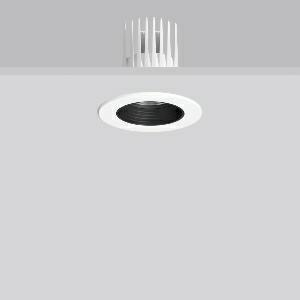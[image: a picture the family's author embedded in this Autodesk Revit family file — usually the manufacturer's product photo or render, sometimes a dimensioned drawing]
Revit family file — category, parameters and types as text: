
# Revit family: heledon_mini_e_901745_002_1_7fe4
name_source: partatom
category: Lighting Fixtures
units: mm (PartAtom-declared; Revit-internal decimal feet)

## family parameters
Cut with Voids When Loaded = No
Host = Face
Light Source = No
Part Type = Normal
Room Calculation Point = No
Round Connector Dimension = Use Diameter
Shared = No

## types (1)
- HELEDON mini E (1 x LED Modul 940, 2150 lm, 4000)
    Apparent Load = 20 VA
    Approval mark = CE
    CIE Flux Codes = 98 100 100 100 100
    Color Rendering = 92
    Color Temperature = 4000
    Default Elevation = 1800 mm
    Description = Series: HELEDON mini
Round recessed downlight. Housing: die-cast aluminium, powder-coated. Black plastic ring and recessed LED to prevent glare from the side. Optical assembly with lens made of plastic (polycarbonate) for the best homogeneous light distribution - can be changed without tools. Best colour rendering index Ra>90. Suitable for Recessed ceiling mounting. Installation without tools thanks to spring fastening system. Including separate LED converter with connecting cable 600 mm.High quality converter without flickering and stroboscopic effect. Through-wiring box (5 pole) available as accessory. The following accessories can be mounted without use of tools: interchangeable lenses, decorative glasses, honeycomb louvre, clear and frosted diffusers, white interchangeable plastic ring. 
Colour: traffic white, matt (RAL 9016)
Diameter: 124 mm
Height: 3 mm
Cut-out diameter: 114 mm
Recess height: 170 mm
Luminaire: recess height: 120 mm
Lamp: LED
Socket: without socket
Colour temperature: 4000K
Colour rendering index (CRI): 92
System power: 20 W
Rated luminous flux: 2150 lm
Luminous efficiency: 108 lm/W
Control gear: Regulated power supply
Protection class: II
Type of protection: IP 20
    Height = 0 mm  [stored 0 ft]
    Lamp = 1 x LED Modul 940
    Lamp Light Flux = 2150 lm
    Lamp count = 1
    Length = 124 mm  [stored 0.406824 ft]
    Lifetime = 50000 h
    Luminous efficacy = 108 lm/W
    Manufacturer = RZB
    ModVariant = No
    Model = 901745.002.1
    Mounting Place = Ceiling
    Mounting Type = Recessed
    Number of Poles = 1
    OnlyDefault = Yes
    Power Factor = 1
    Product Name = HELEDON mini E
    Product group = Recessed downlights
    ProductGroupID = 402
    Protection Class = Protection class II
    Protection Degree = IP 20
    RLX_Detail_Level = 1
    RLX_Emergency_Light_Flux = 0 lm
    RLX_Emergency_Type = 0
    RLX_Emergency_Type_DB = No
    RlxData = <blob elided: 124221 chars, md5=559faab9>
    Socket = socket
    Standby Power = 0 W
    System Light Flux = 2150 lm
    System Power = 20 W
    Type Comments = Product without accessories
    Type Image = 901656.002.jpg
    URL = http://relux.com
    VarID = ---
    Voltage = 230 V
    Voltage Range = 220-240 V
    Weight = 0.00 kg
    Width = 0 mm  [stored 0 ft]

note: [stored X ft] marks values corroborated as IEEE doubles in the binary element streams (Revit-internal decimal feet)

## geometry (parser evidence)
native form markers: Blend x4, Sweep x11
no freeform markers — native parametric forms only
